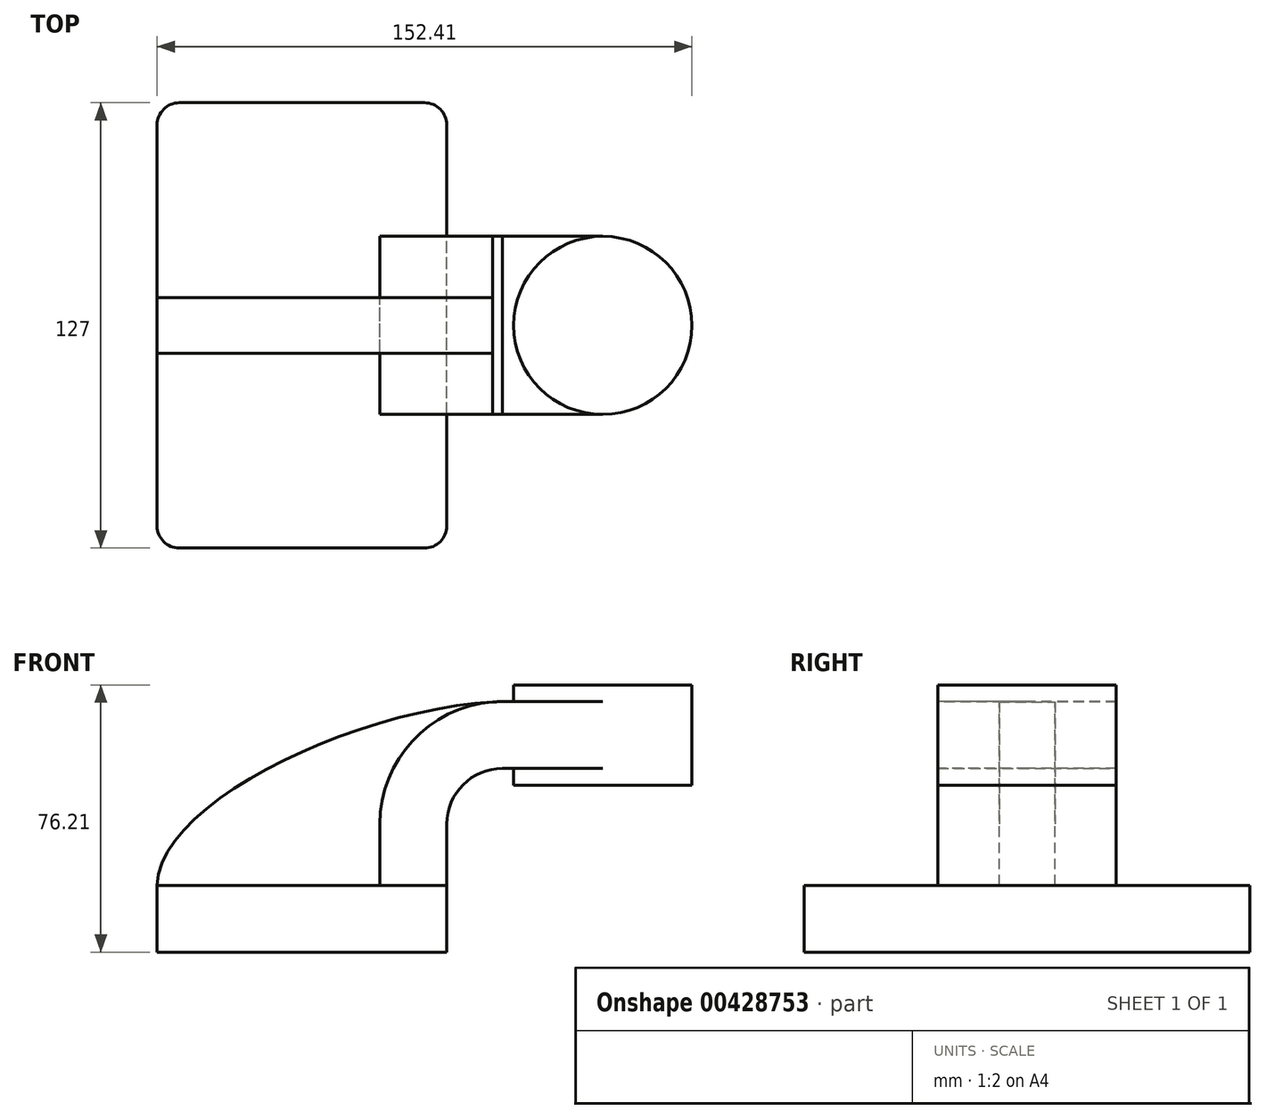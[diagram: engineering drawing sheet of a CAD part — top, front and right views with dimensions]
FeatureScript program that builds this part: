
annotation { "Feature Type Name" : "Feature", "Feature Type Description" : "" }
export const myFeature = defineFeature(function(context is Context, id is Id, definition is map)
    precondition{}
    {
        {
            var Q0;
            Q0=qCreatedBy(makeId("Front.planeOp"),FACE);
            var sketch = newSketch(context, id + "F0", { "sketchPlane" : qUnion([Q0])});
            skLineSegment(sketch, "E0.bottom", {"start": v(41.28, -9.52) * mm, "end": v(-41.28, -9.53) * mm});
            skLineSegment(sketch, "E0.top", {"start": v(41.27, 9.53) * mm, "end": v(-41.28, 9.53) * mm});
            skLineSegment(sketch, "E0.left", {"start": v(41.28, -9.52) * mm, "end": v(41.28, 9.53) * mm});
            skLineSegment(sketch, "E0.right", {"start": v(-41.28, -9.53) * mm, "end": v(-41.28, 9.53) * mm});
            skPoint(sketch, "E0.middle", {"position": v(0, 0) * mm});
            skLineSegment(sketch, "E1.bottom", {"start": v(111.12, 38.1) * mm, "end": v(60.32, 38.1) * mm});
            skLineSegment(sketch, "E1.top", {"start": v(111.12, 66.68) * mm, "end": v(60.32, 66.68) * mm});
            skLineSegment(sketch, "E1.left", {"start": v(111.12, 38.1) * mm, "end": v(111.12, 66.68) * mm});
            skLineSegment(sketch, "E1.right", {"start": v(60.32, 38.1) * mm, "end": v(60.32, 66.67) * mm});
            skPoint(sketch, "E1.middle", {"position": v(85.72, 52.39) * mm});
            skLineSegment(sketch, "E2", {"start": v(41.27, 9.53) * mm, "end": v(41.27, 26.99) * mm});
            skArc(sketch, "E3", {"start": v(41.27, 26.99) * mm, "mid": v(45.92, 38.21) * mm, "end": v(57.15, 42.86) * mm});
            skLineSegment(sketch, "E4", {"start": v(57.15, 42.86) * mm, "end": v(85.72, 42.86) * mm});
            skLineSegment(sketch, "E5.0", {"start": v(57.15, 61.91) * mm, "end": v(85.72, 61.91) * mm});
            skArc(sketch, "E5.1", {"start": v(22.23, 26.99) * mm, "mid": v(32.45, 51.68) * mm, "end": v(57.15, 61.91) * mm});
            skLineSegment(sketch, "E5.2", {"start": v(22.23, 9.53) * mm, "end": v(22.23, 26.99) * mm});
            skLineSegment(sketch, "E6", {"start": v(85.72, 38.1) * mm, "end": v(85.72, 66.68) * mm});
            skFitSpline(sketch, "E7", {"points": [v(-41.28, 9.53) * mm, v(57.15, 61.91) * mm], "startDerivative": vector(1.82, 74.17) * mm, "endDerivative": vector(115.12, 2.83) * mm});
            skSolve(sketch);
        }
        {
            var Q0;
            Q0=makeQuery(id+"F0.imprint","IMPRINT",FACE,{"disambiguationData":[TD([[makeQuery(id+"F0.imprint","IMPRINT",EDGE,{"derivedFrom":sQuery(id+"F0.wireOp",EDGE,"E0.bottom")}),-1.0]])]});
            extrude(context, id + "F1", {"entities" : qUnion([Q0]), "endBound" : BoundingType.SYMMETRIC, "depth" : 127 * mm});
        }
        {
            var Q0;
            {var subQ1=sQuery(id+"F0.wireOp",EDGE,"E2");Q0=makeQuery(id+"F0.imprint","IMPRINT",FACE,{"disambiguationData":[TD([[makeQuery(id+"F0.imprint","IMPRINT",EDGE,{"derivedFrom":subQ1}),1.0]])]});}
            var Q1;
            {var subQ0=sQuery(id+"F0.wireOp",EDGE,"E4");var subQ1=sQuery(id+"F0.wireOp",EDGE,"E1.right");var subQ2=makeQuery(id+"F0.imprint","INTERSECT",VERTEX,{"derivedFrom":[subQ1,subQ0]});Q1=makeQuery(id+"F0.imprint","IMPRINT",FACE,{"disambiguationData":[TD([[makeQuery(id+"F0.imprint","IMPRINT",EDGE,{"disambiguationData":[TD([[subQ2,-1.0]])],"derivedFrom":subQ1}),-1.0]])]});}
            extrude(context, id + "F2", {"entities" : qUnion([Q0, Q1]), "endBound" : BoundingType.SYMMETRIC, "depth" : 50.8 * mm});
        }
        {
            var Q0;
            {var subQ3=sQuery(id+"F0.wireOp",EDGE,"E5.2");Q0=makeQuery(id+"F0.imprint","IMPRINT",FACE,{"disambiguationData":[TD([[makeQuery(id+"F0.imprint","IMPRINT",EDGE,{"derivedFrom":subQ3}),1.0]])]});}
            extrude(context, id + "F3", {"entities" : qUnion([Q0]), "endBound" : BoundingType.SYMMETRIC, "depth" : 15.88 * mm});
        }
        {
            var Q0;
            {var subQ0=sQuery(id+"F0.wireOp",EDGE,"E1.left");Q0=makeQuery(id+"F0.imprint","IMPRINT",FACE,{"disambiguationData":[TD([[makeQuery(id+"F0.imprint","IMPRINT",EDGE,{"derivedFrom":subQ0}),1.0]])]});}
            var Q1;
            Q1=sQuery(id+"F0.wireOp",EDGE,"E6");
            revolve(context, id + "F4", {"operationType" : NewBodyOperationType.ADD, "entities" : qUnion([Q0]), "axis" : qUnion([Q1]), "revolveType" : RevolveType.FULL});
        }
        {
            var Q0;
            Q0=makeQuery(id+"F1.opExtrude","CAP_EDGE",EDGE,{"disambiguationData":[OSD([sQuery(id+"F0.wireOp",EDGE,"E0.left")])],"isStart":false});
            var Q1;
            Q1=makeQuery(id+"F1.opExtrude","CAP_EDGE",EDGE,{"disambiguationData":[OSD([sQuery(id+"F0.wireOp",EDGE,"E0.right")])],"isStart":false});
            var Q2;
            Q2=makeQuery(id+"F1.opExtrude","CAP_EDGE",EDGE,{"disambiguationData":[OSD([sQuery(id+"F0.wireOp",EDGE,"E0.right")])],"isStart":true});
            var Q3;
            Q3=makeQuery(id+"F1.opExtrude","CAP_EDGE",EDGE,{"disambiguationData":[OSD([sQuery(id+"F0.wireOp",EDGE,"E0.left")])],"isStart":true});
            fillet(context, id + "F5", {"entities" : qUnion([Q0, Q1, Q2, Q3]), "radius" : 6.35 * mm, "tangentPropagation" : true, "allowEdgeOverflow" : false});
        }
    });
